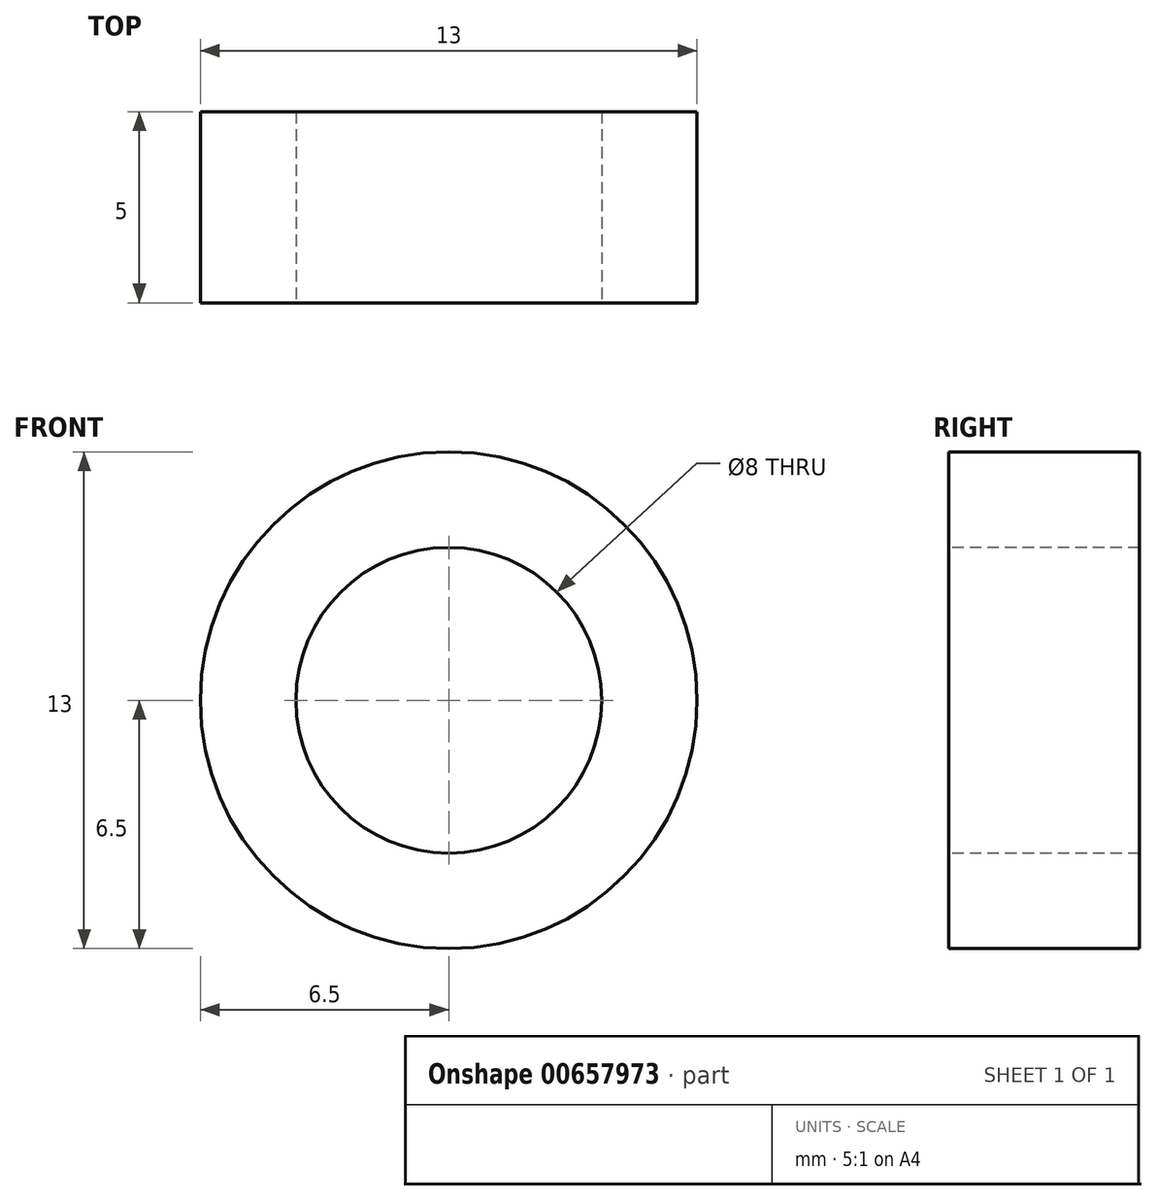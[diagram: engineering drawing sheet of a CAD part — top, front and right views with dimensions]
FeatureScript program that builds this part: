
annotation { "Feature Type Name" : "Feature", "Feature Type Description" : "" }
export const myFeature = defineFeature(function(context is Context, id is Id, definition is map)
    precondition{}
    {
        {
            var Q0;
            Q0=qCreatedBy(makeId("Right.planeOp"),FACE);
            var sketch = newSketch(context, id + "F0", { "sketchPlane" : qUnion([Q0])});
            skLineSegment(sketch, "E0", {"start": v(-2.5, 6.5) * mm, "end": v(-2.5, 4) * mm});
            skLineSegment(sketch, "E1", {"start": v(-2.5, 4) * mm, "end": v(2.5, 4) * mm});
            skLineSegment(sketch, "E2", {"start": v(-2.5, 6.5) * mm, "end": v(2.5, 6.5) * mm});
            skLineSegment(sketch, "E3", {"start": v(2.5, 6.5) * mm, "end": v(2.5, 4) * mm});
            skLineSegment(sketch, "E4", {"start": v(-4.25, 0) * mm, "end": v(4.18, 0) * mm, "construction": true});
            skSolve(sketch);
        }
        {
            var Q0;
            Q0=makeQuery(id+"F0.imprint","IMPRINT",FACE,{"disambiguationData":[TD([[makeQuery(id+"F0.imprint","IMPRINT",EDGE,{"derivedFrom":sQuery(id+"F0.wireOp",EDGE,"E0")}),1.0]])]});
            var Q1;
            Q1=sQuery(id+"F0.wireOp",EDGE,"E4");
            revolve(context, id + "F1", {"entities" : qUnion([Q0]), "axis" : qUnion([Q1]), "revolveType" : RevolveType.FULL});
        }
    });
